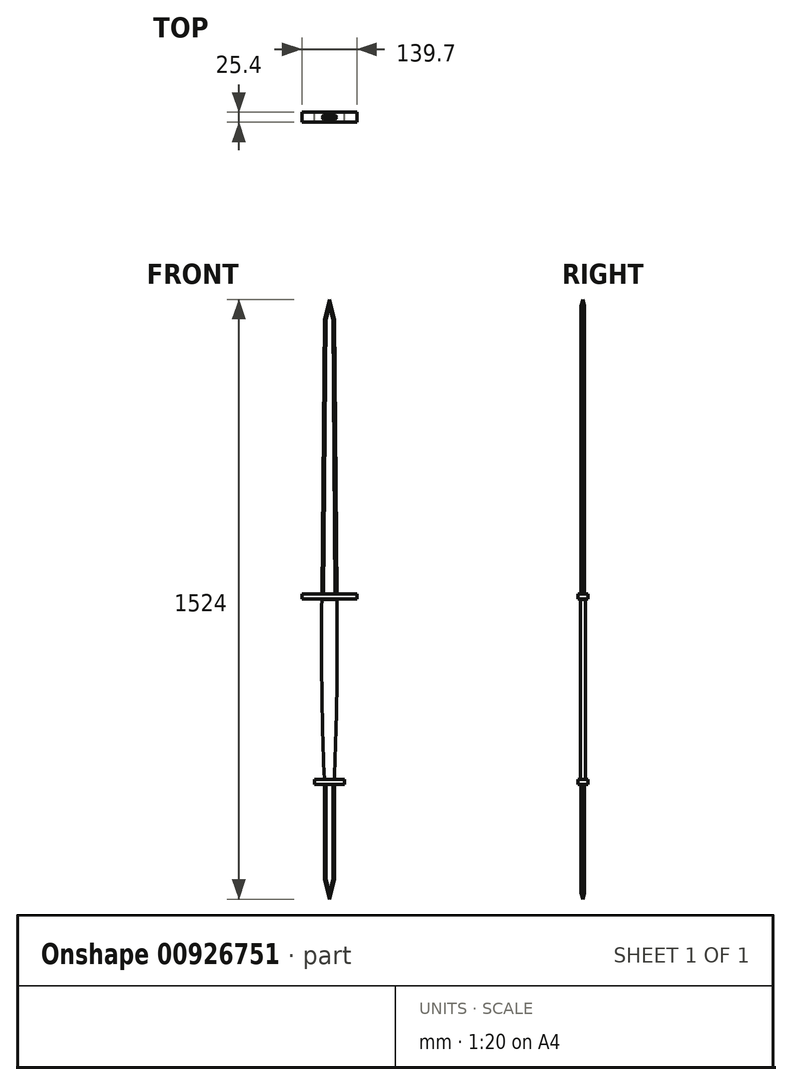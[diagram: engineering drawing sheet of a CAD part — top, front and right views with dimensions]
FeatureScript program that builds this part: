
annotation { "Feature Type Name" : "Feature", "Feature Type Description" : "" }
export const myFeature = defineFeature(function(context is Context, id is Id, definition is map)
    precondition{}
    {
        {
            var Q0;
            Q0=qCreatedBy(makeId("Front.planeOp"),FACE);
            var sketch = newSketch(context, id + "F0", { "sketchPlane" : qUnion([Q0])});
            skLineSegment(sketch, "E0", {"start": v(0, 0) * mm, "end": v(0, -457.2) * mm, "construction": true});
            skLineSegment(sketch, "E1", {"start": v(0, 0) * mm, "end": v(0, 762) * mm, "construction": true});
            skLineSegment(sketch, "E2", {"start": v(0, -457.2) * mm, "end": v(0, -762) * mm, "construction": true});
            skLineSegment(sketch, "E3", {"start": v(0, 0) * mm, "end": v(19.05, 0) * mm});
            skLineSegment(sketch, "E4.MirrorCS", {"start": v(0, 0) * mm, "end": v(-19.05, 0) * mm});
            skPoint(sketch, "E5.visualSharp", {"position": v(-19.05, -467.36) * mm});
            skLineSegment(sketch, "E6", {"start": v(0, -762) * mm, "end": v(0, -711.2) * mm, "construction": true});
            skLineSegment(sketch, "E7", {"start": v(0, -711.2) * mm, "end": v(-12.7, -711.2) * mm, "construction": true});
            skLineSegment(sketch, "E8", {"start": v(-12.7, -711.2) * mm, "end": v(0, -762) * mm});
            skLineSegment(sketch, "E9", {"start": v(-12.7, -711.2) * mm, "end": v(-12.7, -457.2) * mm});
            skLineSegment(sketch, "E10", {"start": v(-12.7, -457.2) * mm, "end": v(0, -457.2) * mm, "construction": true});
            skLineSegment(sketch, "E11", {"start": v(0, 762) * mm, "end": v(0, 711.2) * mm, "construction": true});
            skLineSegment(sketch, "E12", {"start": v(0, 711.2) * mm, "end": v(-12.7, 711.2) * mm, "construction": true});
            skLineSegment(sketch, "E13", {"start": v(0, 762) * mm, "end": v(-12.7, 711.2) * mm});
            skLineSegment(sketch, "E14", {"start": v(-12.7, 711.2) * mm, "end": v(-19.05, 0) * mm});
            skPoint(sketch, "E15.endSnap0", {"position": v(0, -228.6) * mm});
            skArc(sketch, "E16", {"start": v(-19.05, 0) * mm, "mid": v(-19.05, -228.64) * mm, "end": v(-12.7, -457.2) * mm});
            skArc(sketch, "E17.MirrorCS", {"start": v(19.05, 0) * mm, "mid": v(19.05, -228.64) * mm, "end": v(12.7, -457.2) * mm});
            skLineSegment(sketch, "E18.MirrorCS", {"start": v(12.7, 711.2) * mm, "end": v(19.05, 0) * mm});
            skLineSegment(sketch, "E19.MirrorCS", {"start": v(0, 762) * mm, "end": v(12.7, 711.2) * mm});
            skLineSegment(sketch, "E20", {"start": v(-69.85, 0.45) * mm, "end": v(-69.73, 13.15) * mm});
            skLineSegment(sketch, "E21", {"start": v(-12.7, -457.2) * mm, "end": v(12.7, -457.2) * mm});
            skLineSegment(sketch, "E22.MirrorCS", {"start": v(12.7, -711.2) * mm, "end": v(12.7, -457.2) * mm});
            skLineSegment(sketch, "E23.MirrorCS", {"start": v(12.7, -711.2) * mm, "end": v(0, -762) * mm});
            skLineSegment(sketch, "E24.MirrorCS", {"start": v(69.85, 0.45) * mm, "end": v(69.73, 13.15) * mm});
            skLineSegment(sketch, "E25", {"start": v(-69.85, 0.45) * mm, "end": v(69.85, 0.45) * mm});
            skLineSegment(sketch, "E26", {"start": v(-69.73, 13.15) * mm, "end": v(69.73, 13.15) * mm});
            skLineSegment(sketch, "E27", {"start": v(-12.7, -457.2) * mm, "end": v(-38.1, -457.2) * mm, "construction": true});
            skLineSegment(sketch, "E28", {"start": v(-38.1, -457.2) * mm, "end": v(-38.1, -469.9) * mm});
            skLineSegment(sketch, "E29.MirrorCS", {"start": v(38.1, -457.2) * mm, "end": v(38.1, -469.9) * mm});
            skLineSegment(sketch, "E30", {"start": v(-38.1, -457.2) * mm, "end": v(38.1, -457.2) * mm});
            skLineSegment(sketch, "E31", {"start": v(-38.1, -469.9) * mm, "end": v(38.1, -469.9) * mm});
            skSolve(sketch);
        }
        {
            var Q0;
            {var subQ5=sQuery(id+"F0.wireOp",EDGE,"E13");Q0=makeQuery(id+"F0.imprint","IMPRINT",FACE,{"disambiguationData":[TD([[makeQuery(id+"F0.imprint","IMPRINT",EDGE,{"derivedFrom":subQ5}),1.0]])]});}
            extrude(context, id + "F1", {"entities" : qUnion([Q0]), "endBound" : BoundingType.SYMMETRIC, "depth" : 7.94 * mm, "offsetDistance" : 25.4 * mm});
        }
        {
            var Q0;
            {var subQ5=sQuery(id+"F0.wireOp",EDGE,"E20");Q0=makeQuery(id+"F0.imprint","IMPRINT",FACE,{"disambiguationData":[TD([[makeQuery(id+"F0.imprint","IMPRINT",EDGE,{"derivedFrom":subQ5}),-1.0]])]});}
            var Q1;
            {var subQ0=sQuery(id+"F0.wireOp",EDGE,"E26");var subQ1=sQuery(id+"F0.wireOp",EDGE,"E14");var subQ2=makeQuery(id+"F0.imprint","INTERSECT",VERTEX,{"derivedFrom":[subQ1,subQ0]});Q1=makeQuery(id+"F0.imprint","IMPRINT",FACE,{"disambiguationData":[TD([[makeQuery(id+"F0.imprint","IMPRINT",EDGE,{"disambiguationData":[TD([[subQ2,-1.0]])],"derivedFrom":subQ1}),1.0]])]});}
            var Q2;
            {var subQ5=sQuery(id+"F0.wireOp",EDGE,"E24.MirrorCS");Q2=makeQuery(id+"F0.imprint","IMPRINT",FACE,{"disambiguationData":[TD([[makeQuery(id+"F0.imprint","IMPRINT",EDGE,{"derivedFrom":subQ5}),1.0]])]});}
            extrude(context, id + "F2", {"entities" : qUnion([Q0, Q1, Q2]), "endBound" : BoundingType.SYMMETRIC, "depth" : 25.4 * mm, "offsetDistance" : 25.4 * mm});
        }
        {
            var Q0;
            Q0=makeQuery(id+"F0.imprint","IMPRINT",FACE,{"disambiguationData":[TD([[makeQuery(id+"F0.imprint","IMPRINT",EDGE,{"derivedFrom":sQuery(id+"F0.wireOp",EDGE,"E3")}),-1.0]])]});
            extrude(context, id + "F3", {"entities" : qUnion([Q0]), "endBound" : BoundingType.SYMMETRIC, "depth" : 12.7 * mm, "offsetDistance" : 25.4 * mm});
        }
        {
            var Q0;
            {var subQ5=sQuery(id+"F0.wireOp",EDGE,"E28");Q0=makeQuery(id+"F0.imprint","IMPRINT",FACE,{"disambiguationData":[TD([[makeQuery(id+"F0.imprint","IMPRINT",EDGE,{"derivedFrom":subQ5}),1.0]])]});}
            var Q1;
            {var subQ5=sQuery(id+"F0.wireOp",EDGE,"E29.MirrorCS");Q1=makeQuery(id+"F0.imprint","IMPRINT",FACE,{"disambiguationData":[TD([[makeQuery(id+"F0.imprint","IMPRINT",EDGE,{"derivedFrom":subQ5}),-1.0]])]});}
            var Q2;
            {var subQ1=sQuery(id+"F0.wireOp",EDGE,"E9");var subQ3=sQuery(id+"F0.wireOp",EDGE,"E31");var subQ4=makeQuery(id+"F0.imprint","INTERSECT",VERTEX,{"derivedFrom":[subQ1,subQ3]});Q2=makeQuery(id+"F0.imprint","IMPRINT",FACE,{"disambiguationData":[TD([[makeQuery(id+"F0.imprint","IMPRINT",EDGE,{"disambiguationData":[TD([[subQ4,-1.0]])],"derivedFrom":subQ3}),1.0]])]});}
            extrude(context, id + "F4", {"entities" : qUnion([Q0, Q1, Q2]), "endBound" : BoundingType.SYMMETRIC, "depth" : 25.4 * mm, "offsetDistance" : 25.4 * mm});
        }
        {
            var Q0;
            {var subQ5=sQuery(id+"F0.wireOp",EDGE,"E8");Q0=makeQuery(id+"F0.imprint","IMPRINT",FACE,{"disambiguationData":[TD([[makeQuery(id+"F0.imprint","IMPRINT",EDGE,{"derivedFrom":subQ5}),1.0]])]});}
            extrude(context, id + "F5", {"entities" : qUnion([Q0]), "endBound" : BoundingType.SYMMETRIC, "depth" : 7.94 * mm, "offsetDistance" : 25.4 * mm});
        }
        {
            var Q0;
            Q0=makeQuery(id+"F1.opExtrude","CAP_EDGE",EDGE,{"disambiguationData":[OSD([sQuery(id+"F0.wireOp",EDGE,"E18.MirrorCS")])],"isStart":false});
            var Q1;
            Q1=makeQuery(id+"F1.opExtrude","CAP_EDGE",EDGE,{"disambiguationData":[OSD([sQuery(id+"F0.wireOp",EDGE,"E18.MirrorCS")])],"isStart":true});
            var Q2;
            Q2=makeQuery(id+"F1.opExtrude","CAP_EDGE",EDGE,{"disambiguationData":[OSD([sQuery(id+"F0.wireOp",EDGE,"E14")])],"isStart":false});
            var Q3;
            Q3=makeQuery(id+"F1.opExtrude","CAP_EDGE",EDGE,{"disambiguationData":[OSD([sQuery(id+"F0.wireOp",EDGE,"E14")])],"isStart":true});
            chamfer(context, id + "F6", {"entities" : qUnion([Q0, Q1, Q2, Q3]), "width" : 3.96 * mm, "tangentPropagation" : true});
        }
        {
            var Q0;
            Q0=makeQuery(id+"F1.opExtrude","CAP_EDGE",EDGE,{"disambiguationData":[OSD([sQuery(id+"F0.wireOp",EDGE,"E19.MirrorCS")])],"isStart":false});
            var Q1;
            Q1=makeQuery(id+"F1.opExtrude","CAP_EDGE",EDGE,{"disambiguationData":[OSD([sQuery(id+"F0.wireOp",EDGE,"E13")])],"isStart":false});
            var Q2;
            Q2=makeQuery(id+"F1.opExtrude","CAP_EDGE",EDGE,{"disambiguationData":[OSD([sQuery(id+"F0.wireOp",EDGE,"E13")])],"isStart":true});
            var Q3;
            Q3=makeQuery(id+"F1.opExtrude","CAP_EDGE",EDGE,{"disambiguationData":[OSD([sQuery(id+"F0.wireOp",EDGE,"E19.MirrorCS")])],"isStart":true});
            chamfer(context, id + "F7", {"entities" : qUnion([Q0, Q1, Q2, Q3]), "width" : 3.96 * mm, "tangentPropagation" : true});
        }
        {
            var Q0;
            Q0=makeQuery(id+"F5.opExtrude","CAP_EDGE",EDGE,{"disambiguationData":[OSD([sQuery(id+"F0.wireOp",EDGE,"E23.MirrorCS")])],"isStart":false});
            var Q1;
            Q1=makeQuery(id+"F5.opExtrude","CAP_EDGE",EDGE,{"disambiguationData":[OSD([sQuery(id+"F0.wireOp",EDGE,"E22.MirrorCS")])],"isStart":false});
            var Q2;
            Q2=makeQuery(id+"F5.opExtrude","CAP_EDGE",EDGE,{"disambiguationData":[OSD([sQuery(id+"F0.wireOp",EDGE,"E22.MirrorCS")])],"isStart":true});
            var Q3;
            Q3=makeQuery(id+"F5.opExtrude","CAP_EDGE",EDGE,{"disambiguationData":[OSD([sQuery(id+"F0.wireOp",EDGE,"E23.MirrorCS")])],"isStart":true});
            var Q4;
            Q4=makeQuery(id+"F5.opExtrude","CAP_EDGE",EDGE,{"disambiguationData":[OSD([sQuery(id+"F0.wireOp",EDGE,"E8")])],"isStart":false});
            var Q5;
            Q5=makeQuery(id+"F5.opExtrude","CAP_EDGE",EDGE,{"disambiguationData":[OSD([sQuery(id+"F0.wireOp",EDGE,"E8")])],"isStart":true});
            var Q6;
            Q6=makeQuery(id+"F5.opExtrude","CAP_EDGE",EDGE,{"disambiguationData":[OSD([sQuery(id+"F0.wireOp",EDGE,"E9")])],"isStart":false});
            var Q7;
            Q7=makeQuery(id+"F5.opExtrude","CAP_EDGE",EDGE,{"disambiguationData":[OSD([sQuery(id+"F0.wireOp",EDGE,"E9")])],"isStart":true});
            chamfer(context, id + "F8", {"entities" : qUnion([Q0, Q1, Q2, Q3, Q4, Q5, Q6, Q7]), "width" : 3.96 * mm});
        }
        {
            var Q0;
            Q0=makeQuery(id+"F3.opExtrude","CAP_EDGE",EDGE,{"disambiguationData":[OSD([sQuery(id+"F0.wireOp",EDGE,"E17.MirrorCS")])],"isStart":false});
            var Q1;
            Q1=makeQuery(id+"F3.opExtrude","CAP_EDGE",EDGE,{"disambiguationData":[OSD([sQuery(id+"F0.wireOp",EDGE,"E17.MirrorCS")])],"isStart":true});
            var Q2;
            Q2=makeQuery(id+"F3.opExtrude","CAP_EDGE",EDGE,{"disambiguationData":[OSD([sQuery(id+"F0.wireOp",EDGE,"E16")])],"isStart":false});
            var Q3;
            Q3=makeQuery(id+"F3.opExtrude","CAP_EDGE",EDGE,{"disambiguationData":[OSD([sQuery(id+"F0.wireOp",EDGE,"E16")])],"isStart":true});
            fillet(context, id + "F9", {"entities" : qUnion([Q0, Q1, Q2, Q3]), "radius" : 6.35 * mm, "tangentPropagation" : true, "allowEdgeOverflow" : false});
        }
    });
